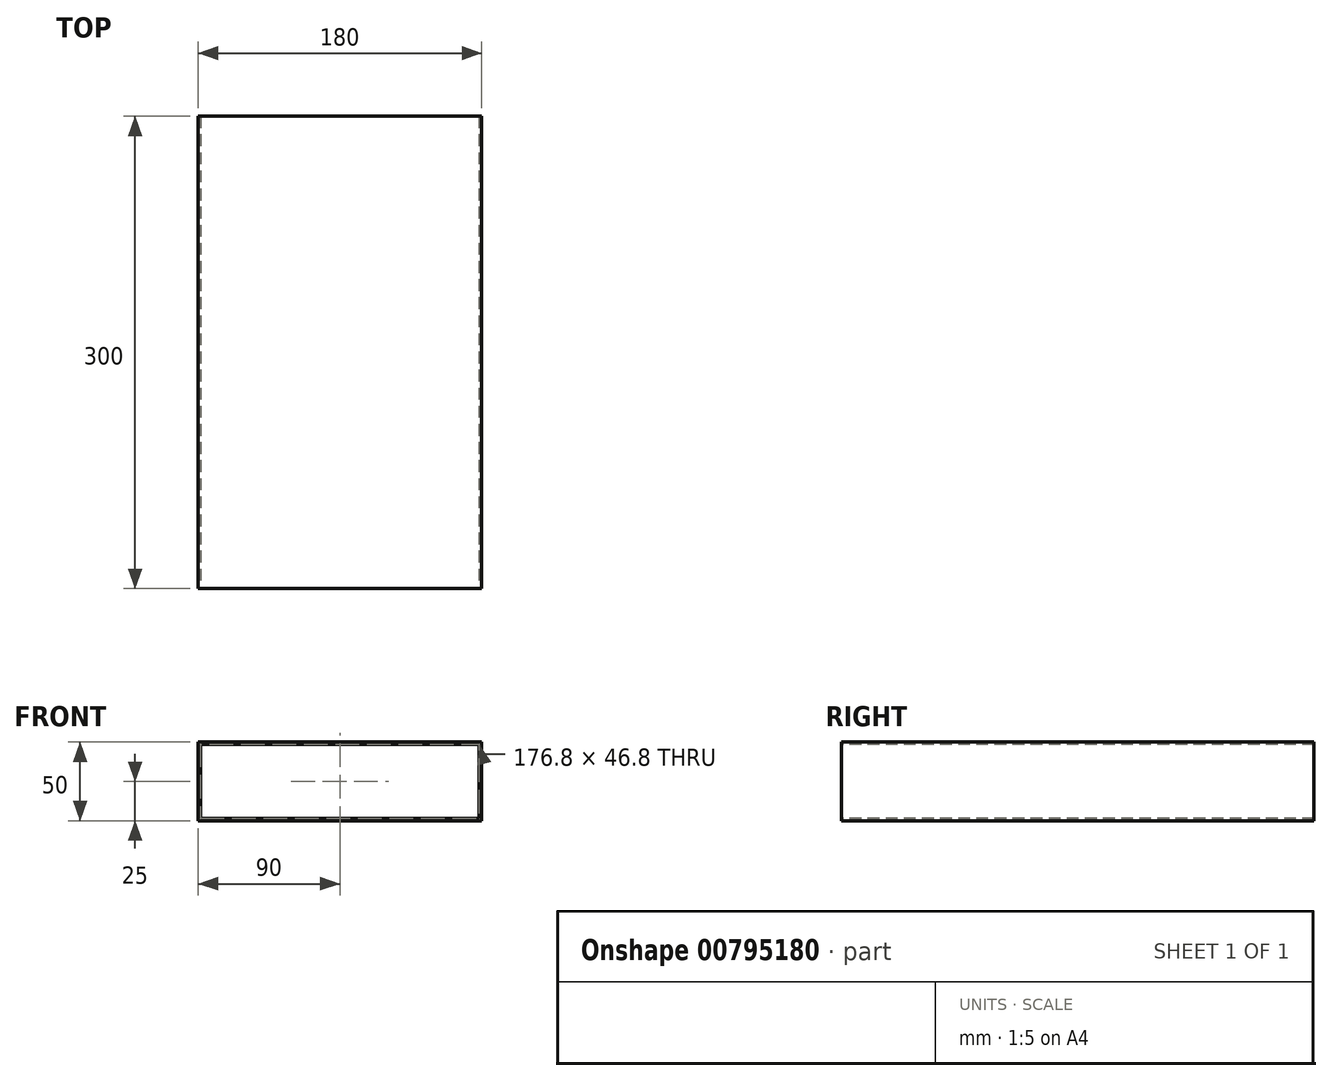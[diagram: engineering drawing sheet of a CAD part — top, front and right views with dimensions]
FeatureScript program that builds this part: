
annotation { "Feature Type Name" : "Feature", "Feature Type Description" : "" }
export const myFeature = defineFeature(function(context is Context, id is Id, definition is map)
    precondition{}
    {
        {
            var Q0;
            Q0=qCreatedBy(makeId("Front.planeOp"),FACE);
            var sketch = newSketch(context, id + "F0", { "sketchPlane" : qUnion([Q0])});
            skLineSegment(sketch, "E0.bottom", {"start": v(0, 0) * mm, "end": v(0, 0) * mm});
            skLineSegment(sketch, "E0.top", {"start": v(0, 0) * mm, "end": v(0, 0) * mm});
            skLineSegment(sketch, "E0.left", {"start": v(0, 0) * mm, "end": v(0, 0) * mm});
            skLineSegment(sketch, "E0.right", {"start": v(0, 0) * mm, "end": v(0, 0) * mm});
            skPoint(sketch, "E0.middle", {"position": v(0, 0) * mm});
            skLineSegment(sketch, "E1.bottom", {"start": v(90, -25) * mm, "end": v(-90, -25) * mm});
            skLineSegment(sketch, "E1.top", {"start": v(90, 25) * mm, "end": v(-90, 25) * mm});
            skLineSegment(sketch, "E1.left", {"start": v(90, -25) * mm, "end": v(90, 25) * mm});
            skLineSegment(sketch, "E1.right", {"start": v(-90, -25) * mm, "end": v(-90, 25) * mm});
            skLineSegment(sketch, "E2.0", {"start": v(-88.4, -23.4) * mm, "end": v(-88.4, 23.4) * mm});
            skLineSegment(sketch, "E2.1", {"start": v(88.4, -23.4) * mm, "end": v(-88.4, -23.4) * mm});
            skLineSegment(sketch, "E2.2", {"start": v(88.4, -23.4) * mm, "end": v(88.4, 23.4) * mm});
            skLineSegment(sketch, "E2.3", {"start": v(88.4, 23.4) * mm, "end": v(-88.4, 23.4) * mm});
            skSolve(sketch);
        }
        {
            var Q0;
            Q0=makeQuery(id+"F0.imprint","IMPRINT",FACE,{"disambiguationData":[TD([[makeQuery(id+"F0.imprint","IMPRINT",EDGE,{"derivedFrom":sQuery(id+"F0.wireOp",EDGE,"E1.bottom")}),-1.0]])]});
            extrude(context, id + "F1", {"entities" : qUnion([Q0]), "oppositeDirection" : true, "depth" : 300 * mm, "offsetDistance" : 25 * mm});
        }
    });
